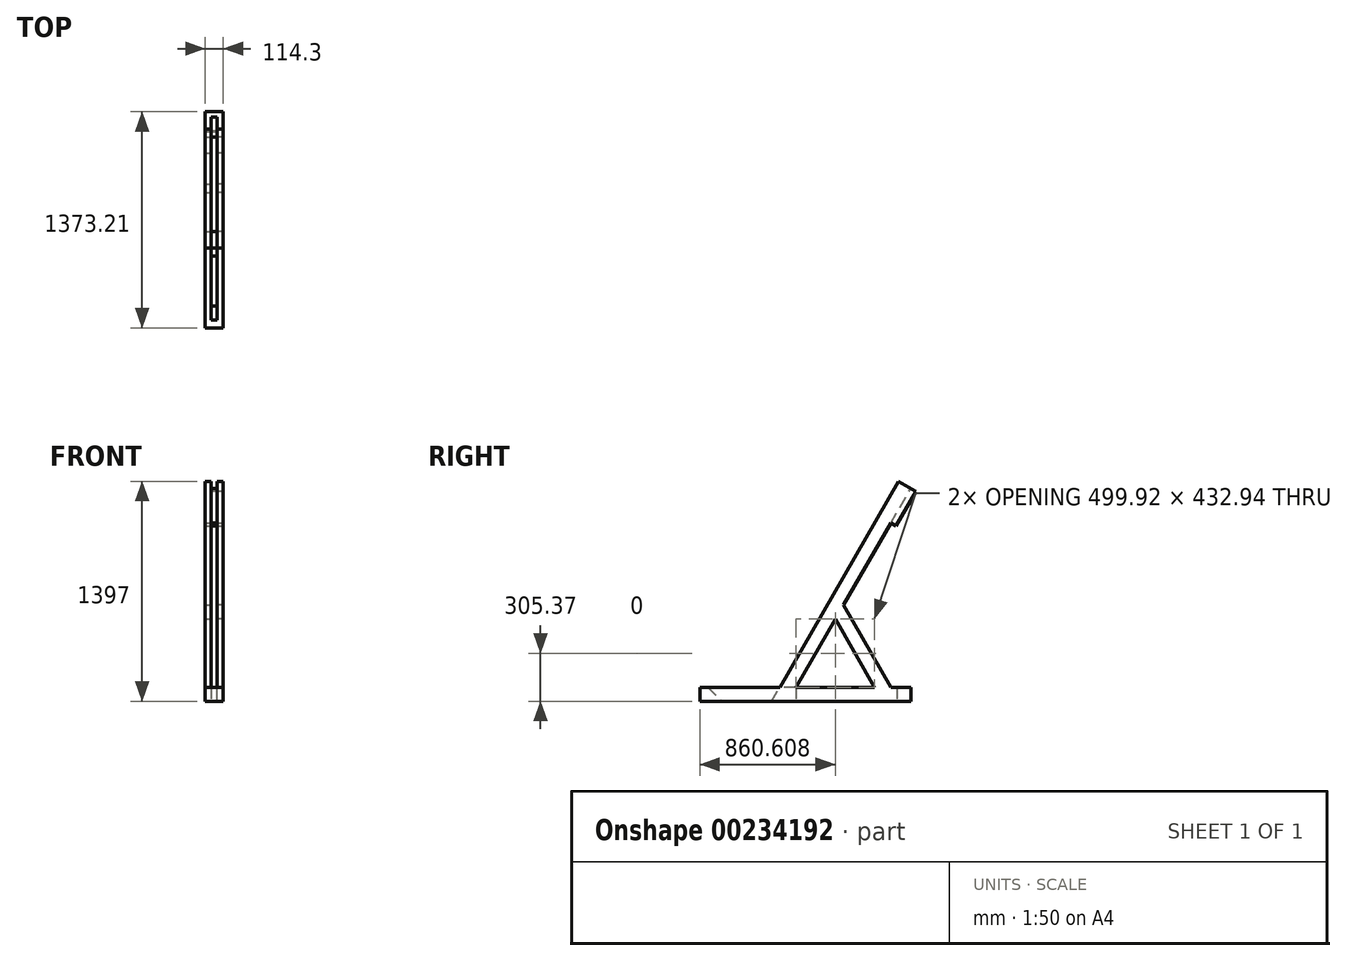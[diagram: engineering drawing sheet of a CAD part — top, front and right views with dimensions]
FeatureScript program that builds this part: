
annotation { "Feature Type Name" : "Feature", "Feature Type Description" : "" }
export const myFeature = defineFeature(function(context is Context, id is Id, definition is map)
    precondition{}
    {
        {
            var Q0;
            Q0=qCreatedBy(makeId("Right.planeOp"),FACE);
            var sketch = newSketch(context, id + "F0", { "sketchPlane" : qUnion([Q0])});
            skLineSegment(sketch, "E0", {"start": v(652.58, 1308.1) * mm, "end": v(-102.65, 0) * mm});
            skLineSegment(sketch, "E1", {"start": v(-102.65, 0) * mm, "end": v(-610.65, 0) * mm});
            skLineSegment(sketch, "E2", {"start": v(-610.65, 0) * mm, "end": v(-610.65, -88.9) * mm});
            skLineSegment(sketch, "E3", {"start": v(-610.65, -88.9) * mm, "end": v(729.57, -88.9) * mm});
            skLineSegment(sketch, "E4", {"start": v(729.57, -88.9) * mm, "end": v(729.57, 0) * mm});
            skLineSegment(sketch, "E5", {"start": v(729.57, 0) * mm, "end": v(602.57, 0) * mm});
            skLineSegment(sketch, "E6", {"start": v(602.57, 0) * mm, "end": v(301.28, 521.84) * mm});
            skLineSegment(sketch, "E7", {"start": v(301.28, 521.84) * mm, "end": v(729.57, 1263.65) * mm});
            skLineSegment(sketch, "E8", {"start": v(729.57, 1263.65) * mm, "end": v(652.58, 1308.1) * mm});
            skLineSegment(sketch, "E9", {"start": v(0, 0) * mm, "end": v(499.92, 0) * mm});
            skLineSegment(sketch, "E10", {"start": v(499.92, 0) * mm, "end": v(249.96, 432.94) * mm});
            skLineSegment(sketch, "E11", {"start": v(249.96, 432.94) * mm, "end": v(0, 0) * mm});
            skLineSegment(sketch, "E12", {"start": v(301.28, 521.84) * mm, "end": v(249.96, 432.94) * mm, "construction": true});
            skLineSegment(sketch, "E13", {"start": v(729.57, 1263.65) * mm, "end": v(729.57, 0) * mm, "construction": true});
            skLineSegment(sketch, "E14", {"start": v(374.94, 216.47) * mm, "end": v(451.93, 260.92) * mm, "construction": true});
            skSolve(sketch);
        }
        {
            var Q0;
            Q0=qCreatedBy(makeId("Right.planeOp"),FACE);
            cPlane(context, id + "F1", {"entities" : qUnion([Q0]), "cplaneType" : CPlaneType.OFFSET, "offset" : 19.05 * mm, "width" : 152.4 * mm, "height" : 152.4 * mm});
        }
        {
            var Q0;
            Q0=qCreatedBy(id+"F1.planeOp",FACE);
            var sketch = newSketch(context, id + "F2", { "sketchPlane" : qUnion([Q0])});
            skLineSegment(sketch, "E15.0", {"start": v(652.58, 1308.1) * mm, "end": v(-102.65, 0) * mm});
            skLineSegment(sketch, "E15.1", {"start": v(-102.65, 0) * mm, "end": v(-610.65, 0) * mm});
            skLineSegment(sketch, "E15.2", {"start": v(-610.65, 0) * mm, "end": v(-610.65, -88.9) * mm});
            skLineSegment(sketch, "E15.3", {"start": v(-610.65, -88.9) * mm, "end": v(729.57, -88.9) * mm});
            skLineSegment(sketch, "E15.4", {"start": v(729.57, -88.9) * mm, "end": v(729.57, 0) * mm});
            skLineSegment(sketch, "E15.5", {"start": v(729.57, 0) * mm, "end": v(602.57, 0) * mm});
            skLineSegment(sketch, "E15.6", {"start": v(602.57, 0) * mm, "end": v(301.28, 521.84) * mm});
            skLineSegment(sketch, "E15.7", {"start": v(301.28, 521.84) * mm, "end": v(729.57, 1263.65) * mm});
            skLineSegment(sketch, "E15.8", {"start": v(729.57, 1263.65) * mm, "end": v(652.58, 1308.1) * mm});
            skLineSegment(sketch, "E15.9", {"start": v(0, 0) * mm, "end": v(499.92, 0) * mm});
            skLineSegment(sketch, "E15.10", {"start": v(499.92, 0) * mm, "end": v(249.96, 432.94) * mm});
            skLineSegment(sketch, "E15.11", {"start": v(249.96, 432.94) * mm, "end": v(0, 0) * mm});
            skSolve(sketch);
        }
        {
            var Q0;
            Q0 = qSketchRegion(id + "F2", true);
            extrude(context, id + "F3", {"entities" : qUnion([Q0]), "depth" : 38.1 * mm});
        }
        {
            var Q0;
            Q0=qCreatedBy(makeId("Right.planeOp"),FACE);
            var sketch = newSketch(context, id + "F4", { "sketchPlane" : qUnion([Q0])});
            skLineSegment(sketch, "E16.0", {"start": v(729.57, -88.9) * mm, "end": v(729.57, 0) * mm});
            skPoint(sketch, "E16.1", {"position": v(-102.65, 0) * mm});
            skLineSegment(sketch, "E16.2", {"start": v(-610.65, 0) * mm, "end": v(-610.65, -88.9) * mm});
            skLineSegment(sketch, "E17", {"start": v(729.57, 0) * mm, "end": v(640.67, 0) * mm});
            skLineSegment(sketch, "E18", {"start": v(640.67, 0) * mm, "end": v(640.67, -88.9) * mm});
            skLineSegment(sketch, "E19", {"start": v(640.67, -88.9) * mm, "end": v(729.57, -88.9) * mm});
            skLineSegment(sketch, "E20", {"start": v(0, 0) * mm, "end": v(0, -88.9) * mm});
            skLineSegment(sketch, "E21", {"start": v(0, -88.9) * mm, "end": v(-153.98, -88.9) * mm});
            skLineSegment(sketch, "E22", {"start": v(-153.98, -88.9) * mm, "end": v(-102.65, 0) * mm});
            skLineSegment(sketch, "E23", {"start": v(0, 0) * mm, "end": v(-102.65, 0) * mm});
            skLineSegment(sketch, "E24", {"start": v(-610.65, 0) * mm, "end": v(-559.85, 0) * mm});
            skLineSegment(sketch, "E25", {"start": v(-559.85, 0) * mm, "end": v(-470.95, -88.9) * mm});
            skLineSegment(sketch, "E26", {"start": v(-470.95, -88.9) * mm, "end": v(-610.65, -88.9) * mm});
            skLineSegment(sketch, "E27.0", {"start": v(729.57, 1263.65) * mm, "end": v(652.58, 1308.1) * mm, "construction": true});
            skLineSegment(sketch, "E28", {"start": v(652.58, 1308.1) * mm, "end": v(608.13, 1231.11) * mm, "construction": true});
            skLineSegment(sketch, "E29", {"start": v(608.13, 1231.11) * mm, "end": v(685.12, 1186.66) * mm, "construction": true});
            skLineSegment(sketch, "E30", {"start": v(685.12, 1186.66) * mm, "end": v(729.57, 1263.65) * mm, "construction": true});
            skSolve(sketch);
        }
        {
            var Q0;
            Q0 = qSketchRegion(id + "F4", true);
            extrude(context, id + "F5", {"entities" : qUnion([Q0]), "operationType" : NewBodyOperationType.ADD, "endBound" : BoundingType.UP_TO_NEXT, "depth" : 25.4 * mm});
        }
        {
            var Q0;
            Q0=makeQuery(id+"F3.opExtrude","SWEPT_BODY",BODY,{"disambiguationData":[OSD([sQuery(id+"F2.wireOp",EDGE,"E15.0"),sQuery(id+"F2.wireOp",EDGE,"E15.1"),sQuery(id+"F2.wireOp",EDGE,"E15.2"),sQuery(id+"F2.wireOp",EDGE,"E15.3"),sQuery(id+"F2.wireOp",EDGE,"E15.4"),sQuery(id+"F2.wireOp",EDGE,"E15.5"),sQuery(id+"F2.wireOp",EDGE,"E15.6"),sQuery(id+"F2.wireOp",EDGE,"E15.7"),sQuery(id+"F2.wireOp",EDGE,"E15.8"),sQuery(id+"F2.wireOp",EDGE,"E15.9"),sQuery(id+"F2.wireOp",EDGE,"E15.10"),sQuery(id+"F2.wireOp",EDGE,"E15.11")])]});
            var Q1;
            Q1=qCreatedBy(makeId("Right.planeOp"),FACE);
            mirror(context, id + "F6", {"operationType" : NewBodyOperationType.ADD, "entities" : qUnion([Q0]), "mirrorPlane" : qUnion([Q1])});
        }
        {
            var Q0;
            Q0=makeQuery(id+"F3.opExtrude","SWEPT_FACE",FACE,{"disambiguationData":[OSD([sQuery(id+"F2.wireOp",EDGE,"E15.7")])]});
            var sketch = newSketch(context, id + "F7", { "sketchPlane" : qUnion([Q0])});
            skLineSegment(sketch, "E31", {"start": v(-57.15, 1459.14) * mm, "end": v(57.15, 1459.14) * mm});
            skLineSegment(sketch, "E32", {"start": v(57.15, 1459.14) * mm, "end": v(57.15, 1205.14) * mm});
            skLineSegment(sketch, "E33", {"start": v(57.15, 1205.14) * mm, "end": v(-57.15, 1205.14) * mm});
            skLineSegment(sketch, "E34", {"start": v(-57.15, 1205.14) * mm, "end": v(-57.15, 1459.14) * mm});
            skSolve(sketch);
        }
        {
            var Q0;
            Q0 = qSketchRegion(id + "F7", true);
            extrude(context, id + "F8", {"entities" : qUnion([Q0]), "operationType" : NewBodyOperationType.ADD, "depth" : 38.1 * mm});
        }
    });
